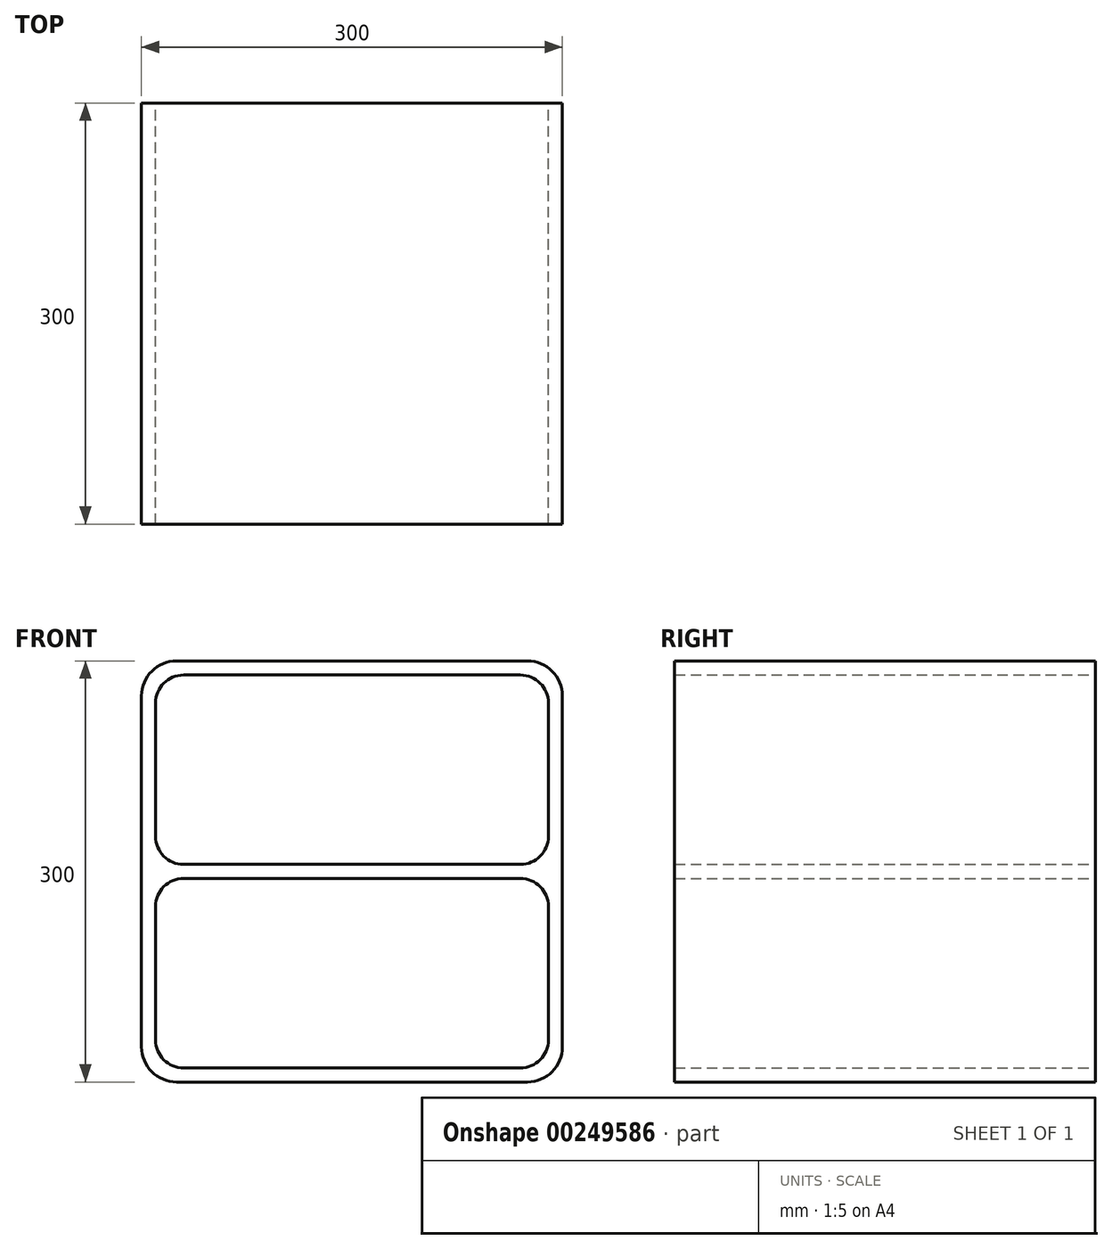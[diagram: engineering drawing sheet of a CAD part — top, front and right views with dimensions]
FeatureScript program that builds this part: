
annotation { "Feature Type Name" : "Feature", "Feature Type Description" : "" }
export const myFeature = defineFeature(function(context is Context, id is Id, definition is map)
    precondition{}
    {
        {
            var Q0;
            Q0=qCreatedBy(makeId("Front.planeOp"),FACE);
            var sketch = newSketch(context, id + "F0", { "sketchPlane" : qUnion([Q0])});
            skLineSegment(sketch, "E0.bottom", {"start": v(0, 0) * mm, "end": v(300, 0) * mm});
            skLineSegment(sketch, "E0.top", {"start": v(0, 300) * mm, "end": v(300, 300) * mm});
            skLineSegment(sketch, "E0.left", {"start": v(0, 0) * mm, "end": v(0, 300) * mm});
            skLineSegment(sketch, "E0.right", {"start": v(300, 0) * mm, "end": v(300, 300) * mm});
            skLineSegment(sketch, "E1.bottom", {"start": v(10, 10) * mm, "end": v(290, 10) * mm});
            skLineSegment(sketch, "E1.top", {"start": v(10, 145) * mm, "end": v(290, 145) * mm});
            skLineSegment(sketch, "E1.left", {"start": v(10, 10) * mm, "end": v(10, 145) * mm});
            skLineSegment(sketch, "E1.right", {"start": v(290, 10) * mm, "end": v(290, 145) * mm});
            skLineSegment(sketch, "E2.bottom", {"start": v(10, 290) * mm, "end": v(290, 290) * mm});
            skLineSegment(sketch, "E2.top", {"start": v(10, 155) * mm, "end": v(290, 155) * mm});
            skLineSegment(sketch, "E2.left", {"start": v(10, 290) * mm, "end": v(10, 155) * mm});
            skLineSegment(sketch, "E2.right", {"start": v(290, 290) * mm, "end": v(290, 155) * mm});
            skSolve(sketch);
        }
        {
            var Q0;
            Q0 = qSketchRegion(id + "F0", true);
            extrude(context, id + "F1", {"entities" : qUnion([Q0]), "depth" : 300 * mm});
        }
        {
            var Q0;
            Q0=makeQuery(id+"F1.opExtrude","SWEPT_EDGE",EDGE,{"disambiguationData":[OSD([sQuery(id+"F0.wireOp",EDGE,"E2.bottom"),sQuery(id+"F0.wireOp",EDGE,"E2.left")])]});
            var Q1;
            Q1=makeQuery(id+"F1.opExtrude","SWEPT_EDGE",EDGE,{"disambiguationData":[OSD([sQuery(id+"F0.wireOp",EDGE,"E1.top"),sQuery(id+"F0.wireOp",EDGE,"E1.left")])]});
            var Q2;
            Q2=makeQuery(id+"F1.opExtrude","SWEPT_EDGE",EDGE,{"disambiguationData":[OSD([sQuery(id+"F0.wireOp",EDGE,"E2.bottom"),sQuery(id+"F0.wireOp",EDGE,"E2.right")])]});
            var Q3;
            Q3=makeQuery(id+"F1.opExtrude","SWEPT_EDGE",EDGE,{"disambiguationData":[OSD([sQuery(id+"F0.wireOp",EDGE,"E1.top"),sQuery(id+"F0.wireOp",EDGE,"E1.right")])]});
            var Q4;
            Q4=makeQuery(id+"F1.opExtrude","SWEPT_EDGE",EDGE,{"disambiguationData":[OSD([sQuery(id+"F0.wireOp",EDGE,"E2.top"),sQuery(id+"F0.wireOp",EDGE,"E2.left")])]});
            var Q5;
            Q5=makeQuery(id+"F1.opExtrude","SWEPT_EDGE",EDGE,{"disambiguationData":[OSD([sQuery(id+"F0.wireOp",EDGE,"E2.top"),sQuery(id+"F0.wireOp",EDGE,"E2.right")])]});
            var Q6;
            Q6=makeQuery(id+"F1.opExtrude","SWEPT_EDGE",EDGE,{"disambiguationData":[OSD([sQuery(id+"F0.wireOp",EDGE,"E1.bottom"),sQuery(id+"F0.wireOp",EDGE,"E1.right")])]});
            var Q7;
            Q7=makeQuery(id+"F1.opExtrude","SWEPT_EDGE",EDGE,{"disambiguationData":[OSD([sQuery(id+"F0.wireOp",EDGE,"E1.bottom"),sQuery(id+"F0.wireOp",EDGE,"E1.left")])]});
            fillet(context, id + "F2", {"entities" : qUnion([Q0, Q1, Q2, Q3, Q4, Q5, Q6, Q7]), "radius" : 20 * mm, "tangentPropagation" : true, "allowEdgeOverflow" : false});
        }
        {
            var Q0;
            Q0=makeQuery(id+"F1.opExtrude","SWEPT_EDGE",EDGE,{"disambiguationData":[OSD([sQuery(id+"F0.wireOp",EDGE,"E0.top"),sQuery(id+"F0.wireOp",EDGE,"E0.left")])]});
            var Q1;
            Q1=makeQuery(id+"F1.opExtrude","SWEPT_EDGE",EDGE,{"disambiguationData":[OSD([sQuery(id+"F0.wireOp",EDGE,"E0.top"),sQuery(id+"F0.wireOp",EDGE,"E0.right")])]});
            var Q2;
            Q2=makeQuery(id+"F1.opExtrude","SWEPT_EDGE",EDGE,{"disambiguationData":[OSD([sQuery(id+"F0.wireOp",EDGE,"E0.bottom"),sQuery(id+"F0.wireOp",EDGE,"E0.right")])]});
            var Q3;
            Q3=makeQuery(id+"F1.opExtrude","SWEPT_EDGE",EDGE,{"disambiguationData":[OSD([sQuery(id+"F0.wireOp",EDGE,"E0.bottom"),sQuery(id+"F0.wireOp",EDGE,"E0.left")])]});
            fillet(context, id + "F3", {"entities" : qUnion([Q0, Q1, Q2, Q3]), "radius" : 25 * mm, "tangentPropagation" : true, "allowEdgeOverflow" : false});
        }
    });
